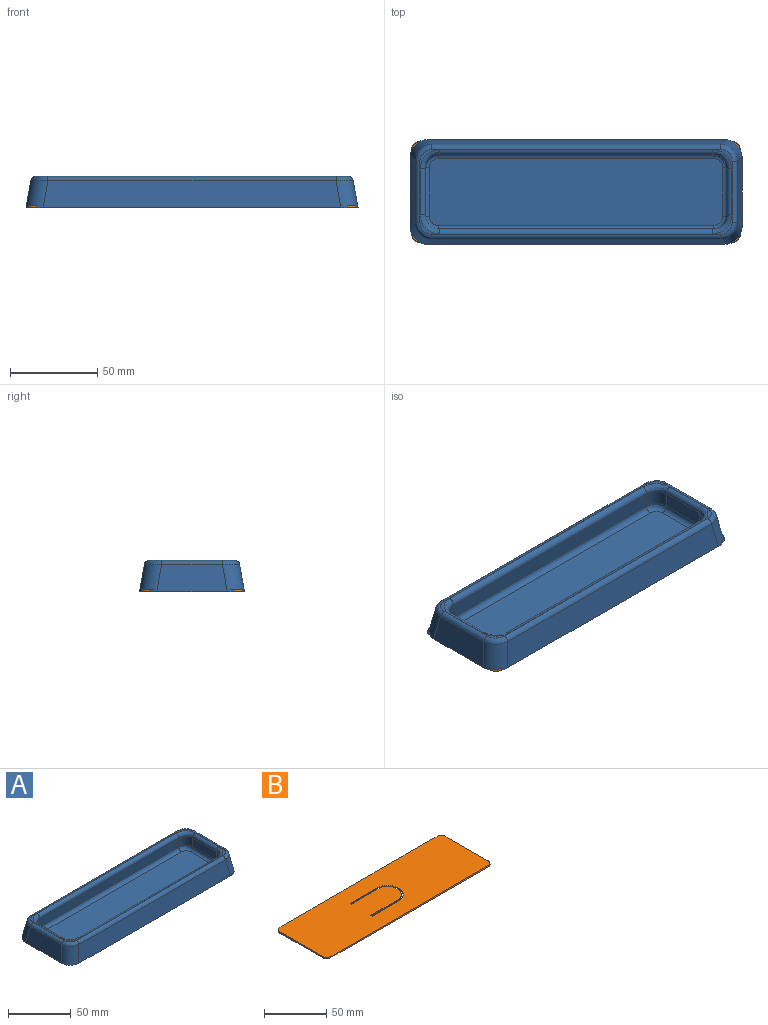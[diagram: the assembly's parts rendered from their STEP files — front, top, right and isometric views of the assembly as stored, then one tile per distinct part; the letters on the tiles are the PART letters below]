
ASSEMBLY  parts=2 mates=1
PART A: 85 faces, bbox 190.2x60.2x18.7 mm
  f0: plane 190x60mm, normal (0,0,-1), area 487.9mm2, adj f2,f3,f4,f5,f15,f16,f17,f18
  f1: plane 178.62x48.62mm, normal (0,0,1), area 157.1mm2, adj f19,f20,f21,f22,f23,f24,f25,f26
  f2: plane 40.3x15.52mm, normal (-0.98,0,0.17), area 592.1mm2, adj f0,f15,f18,f22
  f3: plane 170.3x15.52mm, normal (0,-0.98,0.17), area 2640.9mm2, adj f0,f15,f16,f26
  f4: plane 40.3x15.52mm, normal (0.98,0,0.17), area 592.1mm2, adj f0,f16,f17,f23
  f5: plane 170.3x15.52mm, normal (0,0.98,0.17), area 2640.9mm2, adj f0,f17,f18,f19
  f6: plane 157.94x9.48mm, normal (0,-1,-0.09), area 1494.7mm2, adj f11,f14,f34,f38
  f7: plane 27.94x9.48mm, normal (1,0,-0.09), area 257.9mm2, adj f11,f12,f30,f42
  f8: plane 157.94x9.48mm, normal (0,1,-0.09), area 1494.7mm2, adj f12,f13,f27,f39
  f9: plane 27.94x9.48mm, normal (-1,0,-0.09), area 257.9mm2, adj f13,f14,f31,f35
  f10: plane 167.9x37.9mm, normal (0,0,1), area 6343mm2, adj f35,f36,f37,f38,f39,f40,f41,f42
  f11: cylinder r=8mm len=9.94mm, axis (-0.09,0.09,-0.99), area 117.6mm2, adj f6,f7,f32,f40
  f12: cylinder r=8mm len=9.94mm, axis (-0.09,-0.09,-0.99), area 117.6mm2, adj f7,f8,f28,f41
  f13: cylinder r=8mm len=9.94mm, axis (0.09,-0.09,-0.99), area 117.6mm2, adj f8,f9,f29,f37
  f14: cylinder r=8mm len=9.94mm, axis (0.09,0.09,-0.99), area 117.6mm2, adj f6,f9,f33,f36
  f15: cylinder r=10mm len=16.89mm, axis (-0.17,-0.17,-0.97), area 248.6mm2, adj f0,f2,f3,f24
  f16: cylinder r=10mm len=16.89mm, axis (0.17,-0.17,-0.97), area 248.6mm2, adj f0,f3,f4,f25
  f17: cylinder r=10mm len=16.89mm, axis (0.17,0.17,-0.97), area 248.6mm2, adj f0,f4,f5,f21
  f18: cylinder r=10mm len=16.89mm, axis (-0.17,0.17,-0.97), area 248.6mm2, adj f0,f2,f5,f20
  f19: cylinder r=3mm len=164.83mm, axis (1,0,0), area 690.4mm2, adj f1,f5,f20,f21
  f20: bspline ~9.85x9.85mm, area 55mm2, adj f1,f18,f19,f22
  f21: bspline ~9.85x9.85mm, area 55mm2, adj f1,f17,f19,f23
  f22: cylinder r=3mm len=34.83mm, axis (0,1,0), area 145.9mm2, adj f1,f2,f20,f24
  f23: cylinder r=3mm len=34.83mm, axis (0,1,0), area 145.9mm2, adj f1,f4,f21,f25
  f24: bspline ~9.85x9.85mm, area 55mm2, adj f1,f15,f22,f26
  f25: bspline ~9.85x9.85mm, area 55mm2, adj f1,f16,f23,f26
  f26: cylinder r=3mm len=164.83mm, axis (1,0,0), area 690.4mm2, adj f1,f3,f24,f25
  f27: cylinder r=3mm len=156.28mm, axis (-1,0,0), area 777.4mm2, adj f1,f8,f28,f29
  f28: bspline ~10.96x10.96mm, area 71.2mm2, adj f1,f12,f27,f30
  f29: bspline ~10.96x10.96mm, area 71.2mm2, adj f1,f13,f27,f31
  f30: cylinder r=3mm len=26.28mm, axis (0,1,0), area 130.7mm2, adj f1,f7,f28,f32
  f31: cylinder r=3mm len=26.28mm, axis (0,1,0), area 130.7mm2, adj f1,f9,f29,f33
  f32: bspline ~10.96x10.96mm, area 71.2mm2, adj f1,f11,f30,f34
  f33: bspline ~10.96x10.96mm, area 71.2mm2, adj f1,f14,f31,f34
  f34: cylinder r=3mm len=156.28mm, axis (-1,0,0), area 777.4mm2, adj f1,f6,f32,f33
  f35: cylinder r=3mm len=27.94mm, axis (0,-1,0), area 139mm2, adj f9,f10,f36,f37
  f36: bspline ~7.97x7.97mm, area 55.2mm2, adj f10,f14,f35,f38
  f37: bspline ~7.97x7.97mm, area 55.2mm2, adj f10,f13,f35,f39
  f38: cylinder r=3mm len=157.94mm, axis (1,0,0), area 785.6mm2, adj f6,f10,f36,f40
  f39: cylinder r=3mm len=157.94mm, axis (1,0,0), area 785.6mm2, adj f8,f10,f37,f41
  f40: bspline ~7.97x7.97mm, area 55.2mm2, adj f10,f11,f38,f42
  f41: bspline ~7.97x7.97mm, area 55.2mm2, adj f10,f12,f39,f42
  f42: cylinder r=3mm len=27.94mm, axis (0,-1,0), area 139mm2, adj f7,f10,f40,f41
  f43: plane 178.62x48.62mm, normal (0,0,-1), area 157.1mm2, adj f61,f62,f63,f64,f65,f66,f67,f68
  f44: plane 40.24x15.35mm, normal (0.98,0,-0.17), area 585mm2, adj f0,f57,f60,f64
  f45: plane 170.24x15.35mm, normal (0,0.98,-0.17), area 2610.9mm2, adj f0,f57,f58,f68
  f46: plane 40.24x15.35mm, normal (-0.98,0,-0.17), area 585mm2, adj f0,f58,f59,f65
  f47: plane 170.24x15.35mm, normal (0,-0.98,-0.17), area 2610.9mm2, adj f0,f59,f60,f61
  f48: plane 157.94x9.48mm, normal (0,1,0.09), area 1494.7mm2, adj f53,f56,f76,f80
  f49: plane 27.94x9.48mm, normal (-1,0,0.09), area 257.9mm2, adj f53,f54,f72,f84
  f50: plane 157.94x9.48mm, normal (0,-1,0.09), area 1494.7mm2, adj f54,f55,f69,f81
  f51: plane 27.94x9.48mm, normal (1,0,0.09), area 257.9mm2, adj f55,f56,f73,f77
  f52: plane 167.9x37.9mm, normal (0,0,-1), area 6343mm2, adj f77,f78,f79,f80,f81,f82,f83,f84
  f53: cylinder r=9mm len=9.98mm, axis (-0.09,0.09,-0.99), area 132.3mm2, adj f48,f49,f74,f82
  f54: cylinder r=9mm len=9.98mm, axis (-0.09,-0.09,-0.99), area 132.3mm2, adj f49,f50,f70,f83
  f55: cylinder r=9mm len=9.98mm, axis (0.09,-0.09,-0.99), area 132.3mm2, adj f50,f51,f71,f79
  f56: cylinder r=9mm len=9.98mm, axis (0.09,0.09,-0.99), area 132.3mm2, adj f48,f51,f75,f78
  f57: cylinder r=9mm len=16.58mm, axis (-0.17,-0.17,-0.97), area 220.6mm2, adj f0,f44,f45,f66
  f58: cylinder r=9mm len=16.58mm, axis (0.17,-0.17,-0.97), area 220.6mm2, adj f0,f45,f46,f67
  f59: cylinder r=9mm len=16.58mm, axis (0.17,0.17,-0.97), area 220.6mm2, adj f0,f46,f47,f63
  f60: cylinder r=9mm len=16.58mm, axis (-0.17,0.17,-0.97), area 220.6mm2, adj f0,f44,f47,f62
  f61: cylinder r=2mm len=164.83mm, axis (1,0,0), area 460.3mm2, adj f43,f47,f62,f63
  f62: bspline ~8.86x8.86mm, area 34.2mm2, adj f43,f60,f61,f64
  f63: bspline ~8.86x8.86mm, area 34.2mm2, adj f43,f59,f61,f65
  f64: cylinder r=2mm len=34.83mm, axis (0,1,0), area 97.3mm2, adj f43,f44,f62,f66
  f65: cylinder r=2mm len=34.83mm, axis (0,1,0), area 97.3mm2, adj f43,f46,f63,f67
  f66: bspline ~8.86x8.86mm, area 34.2mm2, adj f43,f57,f64,f68
  f67: bspline ~8.86x8.86mm, area 34.2mm2, adj f43,f58,f65,f68
  f68: cylinder r=2mm len=164.83mm, axis (1,0,0), area 460.3mm2, adj f43,f45,f66,f67
  f69: cylinder r=2mm len=156.28mm, axis (-1,0,0), area 518.3mm2, adj f43,f50,f70,f71
  f70: bspline ~10.96x10.96mm, area 50.9mm2, adj f43,f54,f69,f72
  f71: bspline ~10.96x10.96mm, area 50.9mm2, adj f43,f55,f69,f73
  f72: cylinder r=2mm len=26.28mm, axis (0,1,0), area 87.2mm2, adj f43,f49,f70,f74
  f73: cylinder r=2mm len=26.28mm, axis (0,1,0), area 87.2mm2, adj f43,f51,f71,f75
  f74: bspline ~10.96x10.96mm, area 50.9mm2, adj f43,f53,f72,f76
  f75: bspline ~10.96x10.96mm, area 50.9mm2, adj f43,f56,f73,f76
  f76: cylinder r=2mm len=156.28mm, axis (-1,0,0), area 518.3mm2, adj f43,f48,f74,f75
  f77: cylinder r=4mm len=27.94mm, axis (0,-1,0), area 185.3mm2, adj f51,f52,f78,f79
  f78: bspline ~8.97x8.97mm, area 80.6mm2, adj f52,f56,f77,f80
  f79: bspline ~8.97x8.97mm, area 80.6mm2, adj f52,f55,f77,f81
  f80: cylinder r=4mm len=157.94mm, axis (1,0,0), area 1047.5mm2, adj f48,f52,f78,f82
  f81: cylinder r=4mm len=157.94mm, axis (1,0,0), area 1047.5mm2, adj f50,f52,f79,f83
  f82: bspline ~8.97x8.97mm, area 80.6mm2, adj f52,f53,f80,f84
  f83: bspline ~8.97x8.97mm, area 80.6mm2, adj f52,f54,f81,f84
  f84: cylinder r=4mm len=27.94mm, axis (0,-1,0), area 185.3mm2, adj f49,f52,f82,f83
PART B: 18 faces, bbox 188.1x58.1x1.7 mm
  f0: plane 48.15x1mm, normal (-0.98,0,0.17), area 48.7mm2, adj f4,f5,f14,f17
  f1: plane 178.15x1mm, normal (0,-0.98,0.17), area 180.7mm2, adj f4,f5,f14,f15
  f2: plane 48.15x1mm, normal (0.98,0,0.17), area 48.7mm2, adj f4,f5,f15,f16
  f3: plane 178.15x1mm, normal (0,0.98,0.17), area 180.7mm2, adj f4,f5,f16,f17
  f4: plane 187.65x57.65mm, normal (0,0,1), area 10651.4mm2, adj f0,f1,f2,f3,f6,f7,f8,f9
  f5: plane 188x58mm, normal (0,0,-1), area 10738mm2, adj f0,f1,f2,f3,f6,f7,f8,f9
  f6: plane 30x1mm, normal (0,-1,0), area 30mm2, adj f4,f5,f7,f13
  f7: plane 1.5x1mm, normal (1,0,0), area 1.5mm2, adj f4,f5,f6,f8
  f8: plane 30x1mm, normal (0,1,0), area 30mm2, adj f4,f5,f7,f9
  f9: cylinder r=11mm len=22mm, axis (0,0,1), area 34.6mm2, adj f4,f5,f8,f10
  f10: plane 30x1mm, normal (0,-1,0), area 30mm2, adj f4,f5,f9,f11
  f11: plane 1.5x1mm, normal (1,0,0), area 1.5mm2, adj f4,f5,f10,f12
  f12: plane 30x1mm, normal (0,1,0), area 30mm2, adj f4,f5,f11,f13
  f13: cylinder r=12.5mm len=25mm, axis (0,0,1), area 39.3mm2, adj f4,f5,f6,f12
  f14: cylinder r=5mm len=5.16mm, axis (-0.17,-0.17,-0.97), area 7.9mm2, adj f0,f1,f4,f5
  f15: cylinder r=5mm len=5.16mm, axis (0.17,-0.17,-0.97), area 7.9mm2, adj f1,f2,f4,f5
  f16: cylinder r=5mm len=5.16mm, axis (0.17,0.17,-0.97), area 7.9mm2, adj f2,f3,f4,f5
  f17: cylinder r=5mm len=5.16mm, axis (-0.17,0.17,-0.97), area 7.9mm2, adj f0,f3,f4,f5
PLACE A t=(-49.76,-92.73,-29.48)mm
PLACE B t=(-48.76,-91.72,-29.48)mm
MATE fastened B.f5 <-> A.f0  axis (0,0,-1) through (45.24,-91.72,-29.48)mm
